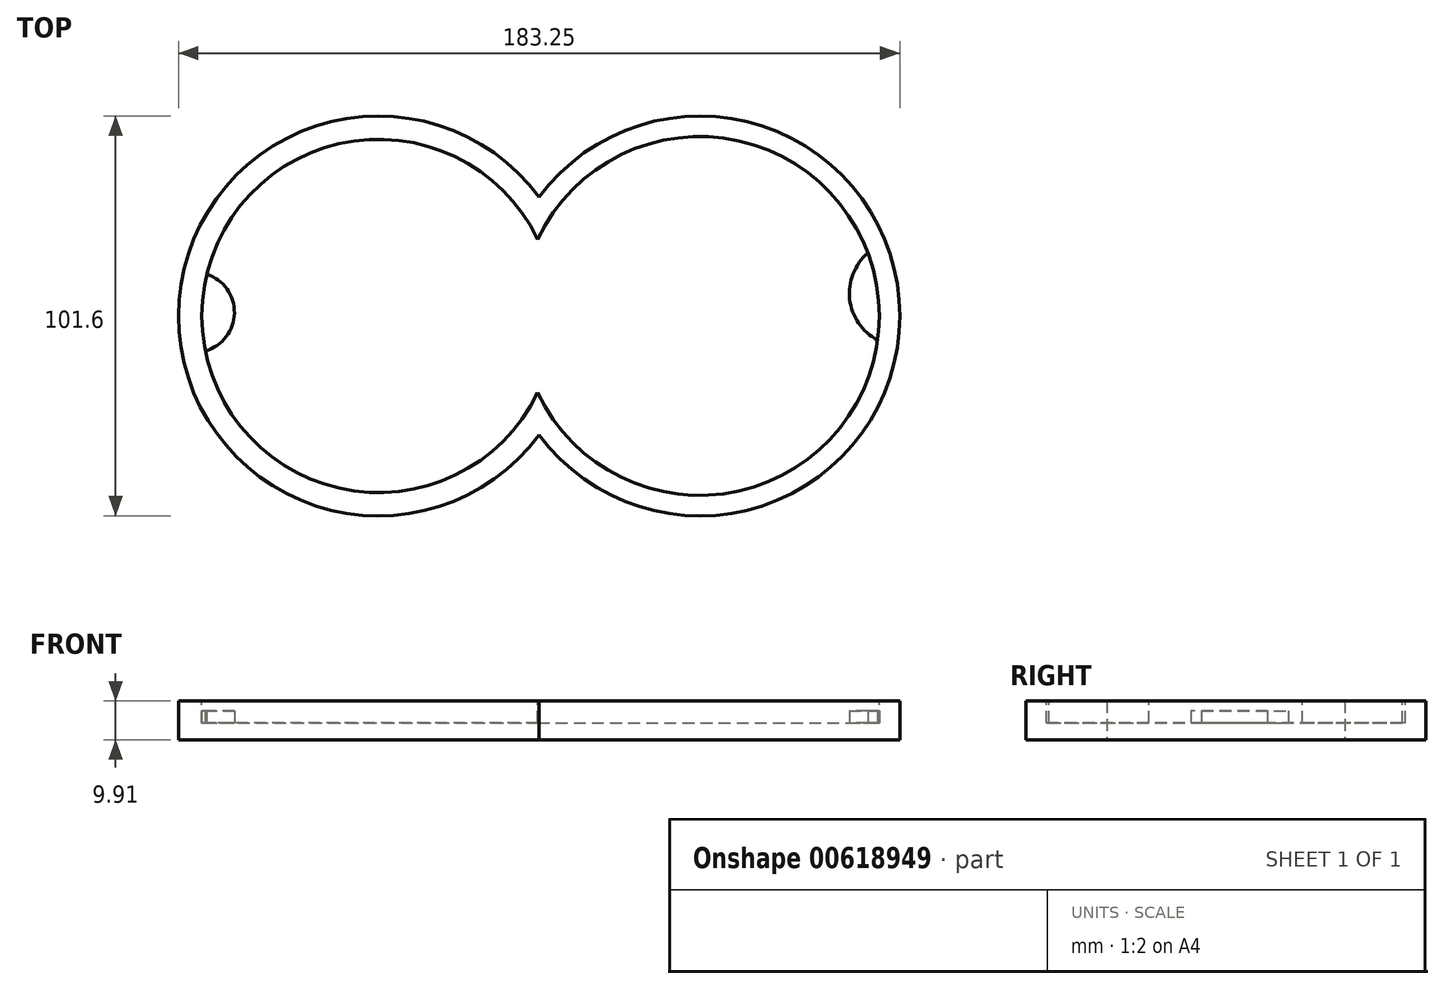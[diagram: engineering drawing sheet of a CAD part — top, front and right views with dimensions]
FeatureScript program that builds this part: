
annotation { "Feature Type Name" : "Feature", "Feature Type Description" : "" }
export const myFeature = defineFeature(function(context is Context, id is Id, definition is map)
    precondition{}
    {
        {
            var Q0;
            Q0=qCreatedBy(makeId("Top.planeOp"),FACE);
            var sketch = newSketch(context, id + "F0", { "sketchPlane" : qUnion([Q0])});
            skCircle(sketch, "E0", {"center": v(-41.36, 0) * mm, "radius": 50.8 * mm});
            skCircle(sketch, "E1", {"center": v(40.29, 0) * mm, "radius": 50.8 * mm});
            skSolve(sketch);
        }
        {
            var Q0;
            {var subQ0=sQuery(id+"F0.wireOp",EDGE,"E1");var subQ1=sQuery(id+"F0.wireOp",EDGE,"E0");var subQ2=makeQuery(id+"F0.imprint","INTERSECT",VERTEX,{"disambiguationData":[OD(0.0)],"derivedFrom":[subQ1,subQ0]});Q0=makeQuery(id+"F0.imprint","IMPRINT",FACE,{"disambiguationData":[TD([[makeQuery(id+"F0.imprint","IMPRINT",EDGE,{"disambiguationData":[TD([[subQ2,1.0]])],"derivedFrom":subQ1}),1.0]])]});}
            var Q1;
            {var subQ0=sQuery(id+"F0.wireOp",EDGE,"E1");var subQ1=sQuery(id+"F0.wireOp",EDGE,"E0");var subQ2=makeQuery(id+"F0.imprint","INTERSECT",VERTEX,{"disambiguationData":[OD(0.0)],"derivedFrom":[subQ1,subQ0]});Q1=makeQuery(id+"F0.imprint","IMPRINT",FACE,{"disambiguationData":[TD([[makeQuery(id+"F0.imprint","IMPRINT",EDGE,{"disambiguationData":[TD([[subQ2,-1.0]])],"derivedFrom":subQ1}),-1.0]])]});}
            var Q2;
            {var subQ0=sQuery(id+"F0.wireOp",EDGE,"E1");var subQ1=sQuery(id+"F0.wireOp",EDGE,"E0");var subQ2=makeQuery(id+"F0.imprint","INTERSECT",VERTEX,{"disambiguationData":[OD(0.0)],"derivedFrom":[subQ1,subQ0]});Q2=makeQuery(id+"F0.imprint","IMPRINT",FACE,{"disambiguationData":[TD([[makeQuery(id+"F0.imprint","IMPRINT",EDGE,{"disambiguationData":[TD([[subQ2,-1.0]])],"derivedFrom":subQ1}),1.0]])]});}
            extrude(context, id + "F1", {"entities" : qUnion([Q0, Q1, Q2]), "depth" : 9.9 * mm, "offsetDistance" : 25.4 * mm});
        }
        {
            var Q0;
            Q0=makeQuery(id+"F1.opExtrude","CAP_FACE",FACE,{"disambiguationData":[OSD([sQuery(id+"F0.wireOp",EDGE,"E0"),sQuery(id+"F0.wireOp",EDGE,"E1")])],"isStart":false});
            var sketch = newSketch(context, id + "F2", { "sketchPlane" : qUnion([Q0])});
            skCircle(sketch, "E2", {"center": v(-41.36, 0) * mm, "radius": 44.88 * mm});
            skCircle(sketch, "E3", {"center": v(40.29, 0) * mm, "radius": 45.58 * mm});
            skSolve(sketch);
        }
        {
            var Q0;
            {var subQ0=sQuery(id+"F2.wireOp",EDGE,"E3");var subQ1=sQuery(id+"F2.wireOp",EDGE,"E2");var subQ2=makeQuery(id+"F2.imprint","INTERSECT",VERTEX,{"disambiguationData":[OD(0.0)],"derivedFrom":[subQ1,subQ0]});Q0=makeQuery(id+"F2.imprint","IMPRINT",FACE,{"disambiguationData":[TD([[makeQuery(id+"F2.imprint","IMPRINT",EDGE,{"disambiguationData":[TD([[subQ2,-1.0]])],"derivedFrom":subQ1}),-1.0]])]});}
            var Q1;
            {var subQ0=sQuery(id+"F2.wireOp",EDGE,"E3");var subQ1=sQuery(id+"F2.wireOp",EDGE,"E2");var subQ2=makeQuery(id+"F2.imprint","INTERSECT",VERTEX,{"disambiguationData":[OD(0.0)],"derivedFrom":[subQ1,subQ0]});Q1=makeQuery(id+"F2.imprint","IMPRINT",FACE,{"disambiguationData":[TD([[makeQuery(id+"F2.imprint","IMPRINT",EDGE,{"disambiguationData":[TD([[subQ2,1.0]])],"derivedFrom":subQ1}),1.0]])]});}
            var Q2;
            {var subQ0=sQuery(id+"F2.wireOp",EDGE,"E3");var subQ1=sQuery(id+"F2.wireOp",EDGE,"E2");var subQ2=makeQuery(id+"F2.imprint","INTERSECT",VERTEX,{"disambiguationData":[OD(0.0)],"derivedFrom":[subQ1,subQ0]});Q2=makeQuery(id+"F2.imprint","IMPRINT",FACE,{"disambiguationData":[TD([[makeQuery(id+"F2.imprint","IMPRINT",EDGE,{"disambiguationData":[TD([[subQ2,-1.0]])],"derivedFrom":subQ1}),1.0]])]});}
            extrude(context, id + "F3", {"entities" : qUnion([Q0, Q1, Q2]), "operationType" : NewBodyOperationType.REMOVE, "oppositeDirection" : true, "depth" : 5.6 * mm, "offsetDistance" : 25.4 * mm});
        }
        {
            var Q0;
            Q0=makeQuery(id+"F3.boolean.opBoolean","COPY",FACE,{"derivedFrom":makeQuery(id+"F3.opExtrude","CAP_FACE",FACE,{"disambiguationData":[OSD([sQuery(id+"F2.wireOp",EDGE,"E2"),sQuery(id+"F2.wireOp",EDGE,"E3")])],"isStart":false})});
            var sketch = newSketch(context, id + "F4", { "sketchPlane" : qUnion([Q0])});
            skArc(sketch, "E4", {"start": v(-85.35, -8.87) * mm, "mid": v(-77.96, 0.72) * mm, "end": v(-84.97, 10.6) * mm});
            skArc(sketch, "E5", {"start": v(82.97, 15.97) * mm, "mid": v(78.35, 4.26) * mm, "end": v(85.45, -6.13) * mm});
            skSolve(sketch);
        }
        {
            var Q0;
            {var subQ0=sQuery(id+"F4.wireOp",EDGE,"E4");Q0=makeQuery(id+"F4.imprint","IMPRINT",FACE,{"disambiguationData":[TD([[makeQuery(id+"F4.imprint","IMPRINT",EDGE,{"derivedFrom":subQ0}),1.0]])]});}
            var Q1;
            {var subQ0=sQuery(id+"F4.wireOp",EDGE,"E5");Q1=makeQuery(id+"F4.imprint","IMPRINT",FACE,{"disambiguationData":[TD([[makeQuery(id+"F4.imprint","IMPRINT",EDGE,{"derivedFrom":subQ0}),1.0]])]});}
            extrude(context, id + "F5", {"entities" : qUnion([Q0, Q1]), "depth" : 3.05 * mm, "offsetDistance" : 25.4 * mm});
        }
    });
